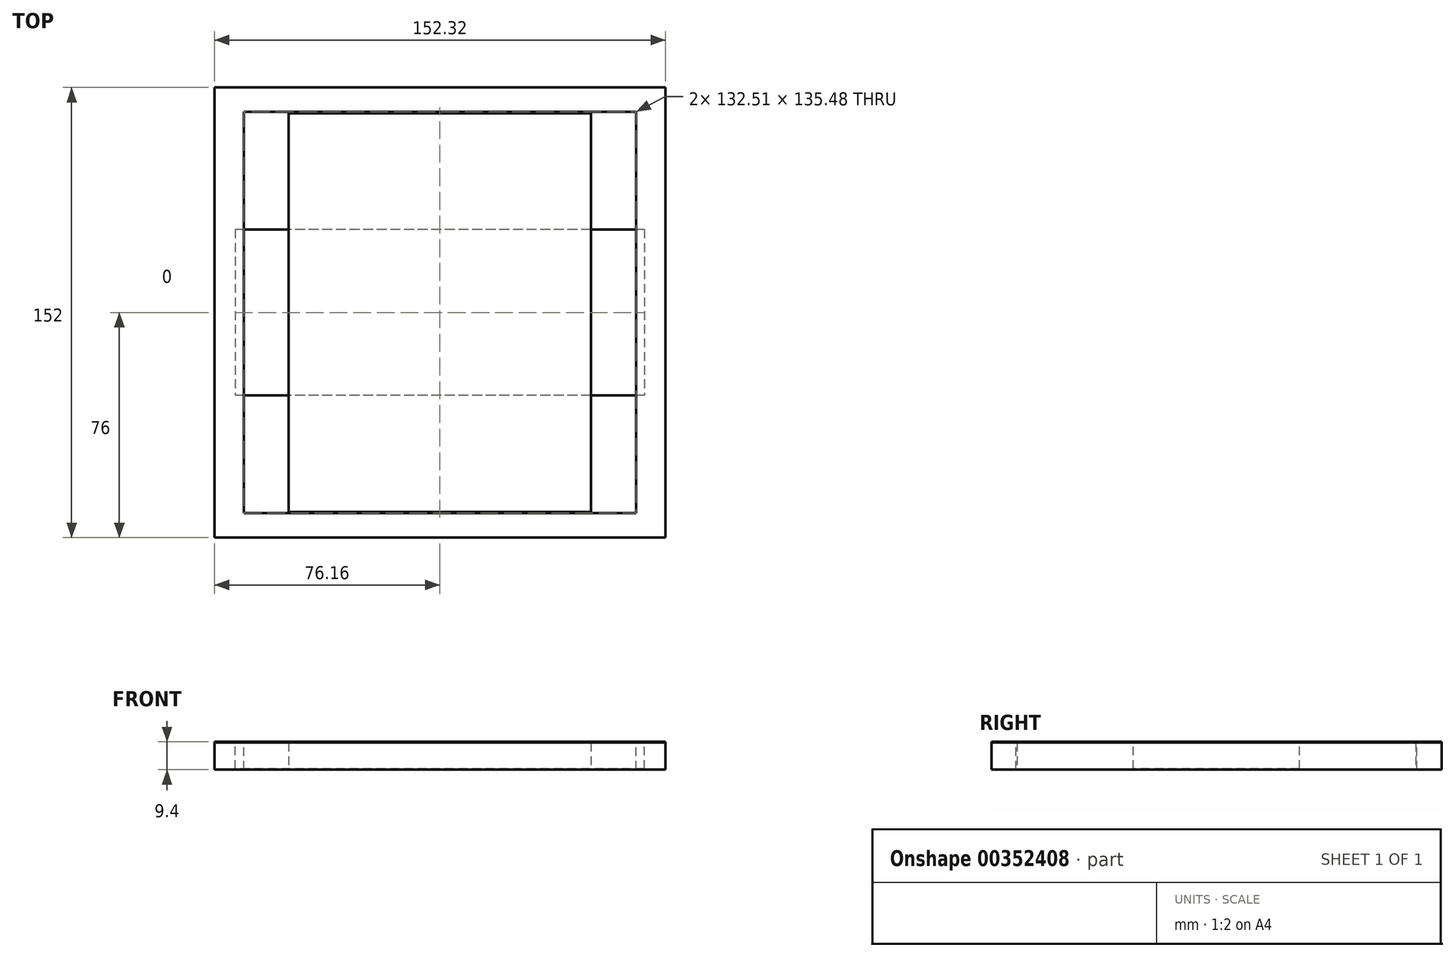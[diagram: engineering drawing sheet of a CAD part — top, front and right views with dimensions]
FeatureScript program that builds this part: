
annotation { "Feature Type Name" : "Feature", "Feature Type Description" : "" }
export const myFeature = defineFeature(function(context is Context, id is Id, definition is map)
    precondition{}
    {
        {
            var Q0;
            Q0=qCreatedBy(makeId("Top.planeOp"),FACE);
            var sketch = newSketch(context, id + "F0", { "sketchPlane" : qUnion([Q0])});
            skLineSegment(sketch, "E0.bottom", {"start": v(76.16, 76) * mm, "end": v(-76.16, 76) * mm});
            skLineSegment(sketch, "E0.top", {"start": v(76.16, -76) * mm, "end": v(-76.16, -76) * mm});
            skLineSegment(sketch, "E0.left", {"start": v(76.16, 76) * mm, "end": v(76.16, -76) * mm});
            skLineSegment(sketch, "E0.right", {"start": v(-76.16, 76) * mm, "end": v(-76.16, -76) * mm});
            skPoint(sketch, "E0.middle", {"position": v(0, 0) * mm});
            skSolve(sketch);
        }
        {
            var Q0;
            Q0=makeQuery(id+"F0.imprint","IMPRINT",FACE,{"disambiguationData":[TD([[makeQuery(id+"F0.imprint","IMPRINT",EDGE,{"derivedFrom":sQuery(id+"F0.wireOp",EDGE,"E0.bottom")}),1.0]])]});
            extrude(context, id + "F1", {"entities" : qUnion([Q0]), "depth" : 9.14 * mm});
        }
        {
            var Q0;
            Q0=makeQuery(id+"F1.opExtrude","CAP_FACE",FACE,{"disambiguationData":[OSD([sQuery(id+"F0.wireOp",EDGE,"E0.bottom"),sQuery(id+"F0.wireOp",EDGE,"E0.top"),sQuery(id+"F0.wireOp",EDGE,"E0.left"),sQuery(id+"F0.wireOp",EDGE,"E0.right")])],"isStart":false});
            var sketch = newSketch(context, id + "F2", { "sketchPlane" : qUnion([Q0])});
            skLineSegment(sketch, "E1.bottom", {"start": v(66.25, 67.74) * mm, "end": v(-66.25, 67.74) * mm});
            skLineSegment(sketch, "E1.top", {"start": v(66.25, -67.74) * mm, "end": v(-66.25, -67.74) * mm});
            skLineSegment(sketch, "E1.left", {"start": v(66.25, 67.74) * mm, "end": v(66.25, -67.74) * mm});
            skLineSegment(sketch, "E1.right", {"start": v(-66.25, 67.74) * mm, "end": v(-66.25, -67.74) * mm});
            skPoint(sketch, "E1.middle", {"position": v(0, 0) * mm});
            skSolve(sketch);
        }
        {
            var Q0;
            Q0=makeQuery(id+"F2.imprint","IMPRINT",FACE,{"disambiguationData":[TD([[makeQuery(id+"F2.imprint","IMPRINT",EDGE,{"derivedFrom":sQuery(id+"F2.wireOp",EDGE,"E1.bottom")}),1.0]])]});
            extrude(context, id + "F3", {"entities" : qUnion([Q0]), "operationType" : NewBodyOperationType.REMOVE, "oppositeDirection" : true, "depth" : 25.4 * mm});
        }
        {
            var Q0;
            Q0=qCreatedBy(makeId("Top.planeOp"),FACE);
            var sketch = newSketch(context, id + "F4", { "sketchPlane" : qUnion([Q0])});
            skLineSegment(sketch, "E2.bottom", {"start": v(51.08, 67.31) * mm, "end": v(-51.08, 67.31) * mm});
            skLineSegment(sketch, "E2.top", {"start": v(51.08, -67.31) * mm, "end": v(-51.08, -67.31) * mm});
            skLineSegment(sketch, "E2.left", {"start": v(51.08, 67.31) * mm, "end": v(51.08, -67.31) * mm});
            skLineSegment(sketch, "E2.right", {"start": v(-51.08, 67.31) * mm, "end": v(-51.08, -67.31) * mm});
            skPoint(sketch, "E2.middle", {"position": v(0, 0) * mm});
            skSolve(sketch);
        }
        {
            var Q0;
            Q0=makeQuery(id+"F4.imprint","IMPRINT",FACE,{"disambiguationData":[TD([[makeQuery(id+"F4.imprint","IMPRINT",EDGE,{"derivedFrom":sQuery(id+"F4.wireOp",EDGE,"E2.bottom")}),1.0]])]});
            extrude(context, id + "F5", {"entities" : qUnion([Q0]), "depth" : 9.14 * mm});
        }
        {
            var Q0;
            Q0=makeQuery(id+"F5.opExtrude","CAP_FACE",FACE,{"disambiguationData":[OSD([sQuery(id+"F4.wireOp",EDGE,"E2.bottom"),sQuery(id+"F4.wireOp",EDGE,"E2.top"),sQuery(id+"F4.wireOp",EDGE,"E2.left"),sQuery(id+"F4.wireOp",EDGE,"E2.right")])],"isStart":false});
            var sketch = newSketch(context, id + "F6", { "sketchPlane" : qUnion([Q0])});
            skLineSegment(sketch, "E3.bottom", {"start": v(69.09, 28.05) * mm, "end": v(-69.09, 28.05) * mm});
            skLineSegment(sketch, "E3.top", {"start": v(69.09, -28.05) * mm, "end": v(-69.09, -28.05) * mm});
            skLineSegment(sketch, "E3.left", {"start": v(69.09, 28.05) * mm, "end": v(69.09, -28.05) * mm});
            skLineSegment(sketch, "E3.right", {"start": v(-69.09, 28.05) * mm, "end": v(-69.09, -28.05) * mm});
            skPoint(sketch, "E3.middle", {"position": v(0, 0) * mm});
            skSolve(sketch);
        }
        {
            var Q0;
            {var subQ0=sQuery(id+"F6.wireOp",EDGE,"E3.right");Q0=makeQuery(id+"F6.imprint","IMPRINT",FACE,{"disambiguationData":[TD([[makeQuery(id+"F6.imprint","IMPRINT",EDGE,{"derivedFrom":subQ0}),1.0]])]});}
            var Q1;
            {var subQ0=sQuery(id+"F6.wireOp",EDGE,"E3.left");Q1=makeQuery(id+"F6.imprint","IMPRINT",FACE,{"disambiguationData":[TD([[makeQuery(id+"F6.imprint","IMPRINT",EDGE,{"derivedFrom":subQ0}),-1.0]])]});}
            var Q2;
            {var subQ0=sQuery(id+"F6.wireOp",EDGE,"E3.bottom");var subQ1=makeQuery(id+"F5.opExtrude","CAP_EDGE",EDGE,{"disambiguationData":[OSD([sQuery(id+"F4.wireOp",EDGE,"E2.left")])],"isStart":false});var subQ2=makeQuery(id+"F6.imprint","INTERSECT",VERTEX,{"derivedFrom":[subQ1,subQ0]});Q2=makeQuery(id+"F6.imprint","IMPRINT",FACE,{"disambiguationData":[TD([[makeQuery(id+"F6.imprint","IMPRINT",EDGE,{"disambiguationData":[TD([[subQ2,-1.0]])],"derivedFrom":subQ0}),1.0]])]});}
            extrude(context, id + "F7", {"entities" : qUnion([Q0, Q1, Q2]), "oppositeDirection" : true, "depth" : 8.9 * mm});
        }
        {
            var Q0;
            Q0=makeQuery(id+"F1.opExtrude","CAP_FACE",FACE,{"disambiguationData":[OSD([sQuery(id+"F0.wireOp",EDGE,"E0.bottom"),sQuery(id+"F0.wireOp",EDGE,"E0.top"),sQuery(id+"F0.wireOp",EDGE,"E0.left"),sQuery(id+"F0.wireOp",EDGE,"E0.right")])],"isStart":false});
            extrude(context, id + "F8", {"entities" : qUnion([Q0]), "depth" : 0.25 * mm});
        }
        {
            var Q0;
            Q0=makeQuery(id+"F5.opExtrude","CAP_FACE",FACE,{"disambiguationData":[OSD([sQuery(id+"F4.wireOp",EDGE,"E2.bottom"),sQuery(id+"F4.wireOp",EDGE,"E2.top"),sQuery(id+"F4.wireOp",EDGE,"E2.left"),sQuery(id+"F4.wireOp",EDGE,"E2.right")])],"isStart":false});
            extrude(context, id + "F9", {"entities" : qUnion([Q0]), "depth" : 0.25 * mm});
        }
    });
